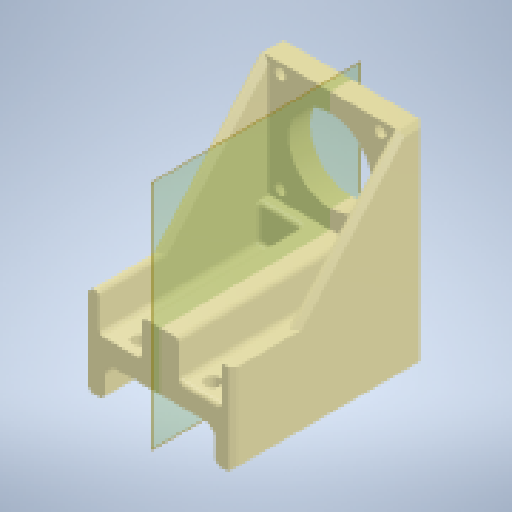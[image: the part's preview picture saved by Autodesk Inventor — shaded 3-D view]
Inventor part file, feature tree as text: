
AUTODESK INVENTOR PART (.ipt)
format: ipt  version: 2023 (Build 270158000, 158)  size: 323,072 bytes
history: native  units: mm
features: extrude x7, sketch x6, fillet x2, projected_geometry x2, plane x1, mirror x1, chamfer x1
ambient origin geometry x8: Origin, YZ Plane, XZ Plane, XY Plane, X Axis, Y Axis, Z Axis, Center Point
bodies: Solid1 (feature_tree)
feature tree (20):
  extrude  "Extrusion1"  Depth=5.0mm
  extrude  "Extrusion2"  Depth=10.0mm TaperAngle=0.0deg
  plane  "Work Plane2"
  mirror  "Mirror2"
  extrude  "Extrusion6"  Depth=5.0mm TaperAngle=0.0deg
  extrude  "Extrusion7"  Depth=15.0mm TaperAngle=0.0deg
  fillet  "Fillet1"  Radius=17.5mm
  extrude  "Extrusion8"  Depth=10.0mm TaperAngle=0.0deg
  extrude  "Extrusion9"  Depth=56.4mm
  chamfer  "Chamfer3"  Distance=50.0mm
  extrude  "Extrusion10"  Depth=56.4mm
  fillet  "Fillet2"  Radius=44.75mm
  sketch  "Sketch2"  dims[d0=47.14mm d1=5.0mm d2=58.0mm]
  projected_geometry  "Projected Loop3"
  sketch  "Sketch7"  dims[d4=39.0mm d5=10.0mm d6=0.0mm]
  sketch  "Sketch8"  dims[d7=50.0mm d8=5.0mm d9=0.0mm]
  sketch  "Sketch9"  dims[d34=55.4mm d35=15.0mm d36=0.0mm d37=17.5mm]
  projected_geometry  "Projected Loop4"
  sketch  "Sketch10"  dims[d38=10.0mm d39=75.0mm d40=0.0mm]
  sketch  "Sketch11"  dims[d41=2.0mm d45=6.7625mm d46=50.0mm d47=34.0mm d49=44.75mm d50=0.0mm d51=51.8mm d52=5.08mm d53=15.5mm d54=2.0mm d55=0.0mm d56=2.0mm d57=2.0mm d58=45.0deg d59=25.0mm d60=22.5mm d61=10.0mm d62=0.0mm d63=2.0mm d64=56.4mm d65=7.5mm]
